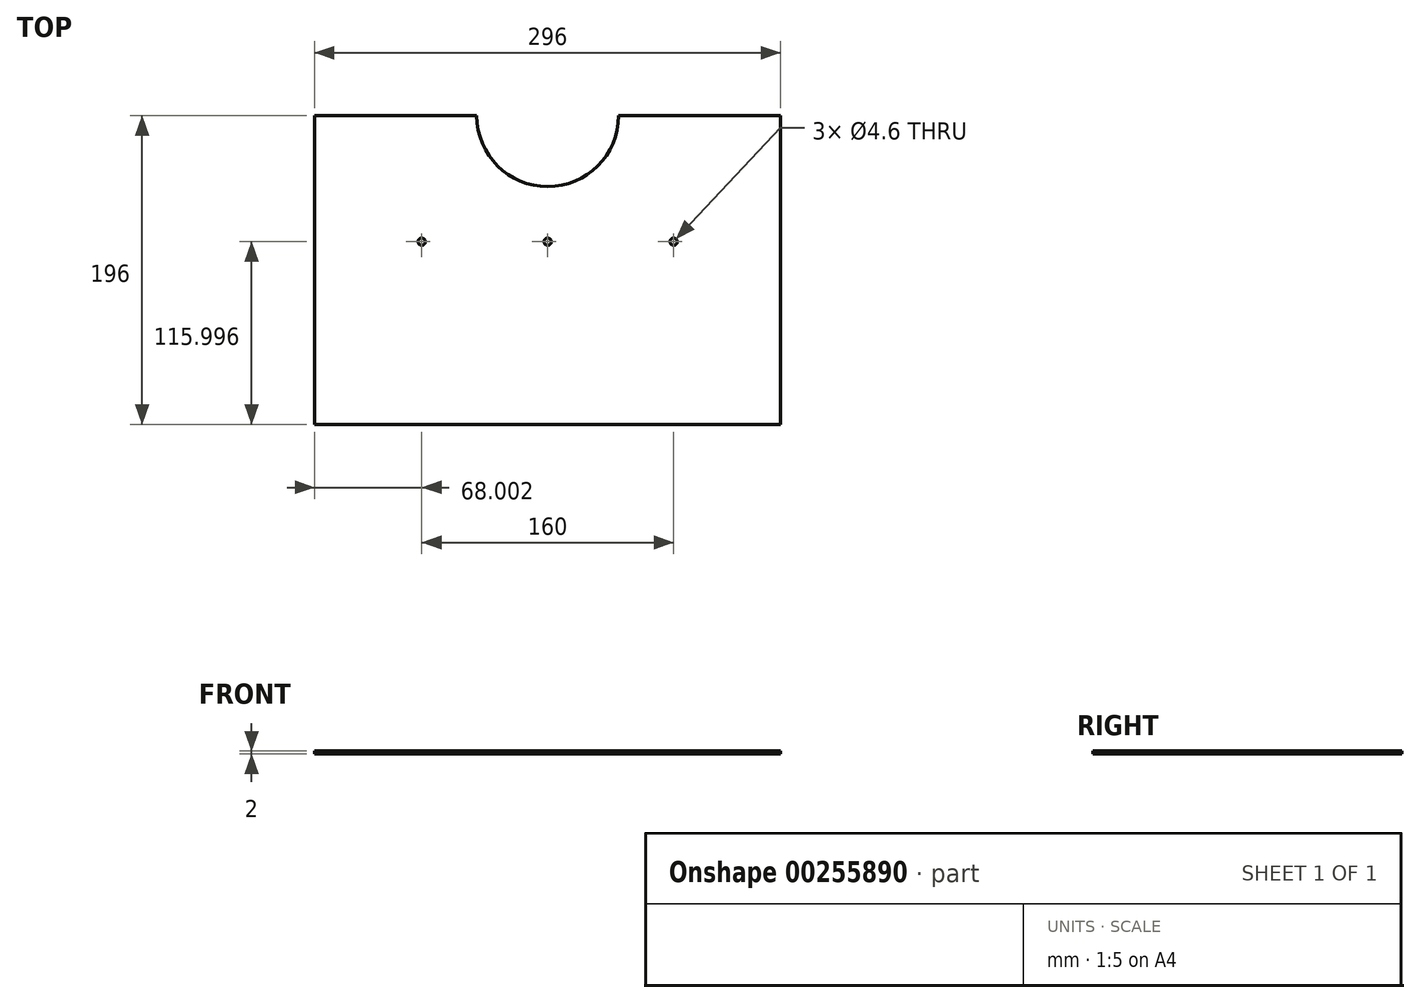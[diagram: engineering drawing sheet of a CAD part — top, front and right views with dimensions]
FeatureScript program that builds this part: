
annotation { "Feature Type Name" : "Feature", "Feature Type Description" : "" }
export const myFeature = defineFeature(function(context is Context, id is Id, definition is map)
    precondition{}
    {
        {
            var Q0;
            Q0=qCreatedBy(makeId("Top.planeOp"),FACE);
            var sketch = newSketch(context, id + "F0", { "sketchPlane" : qUnion([Q0])});
            skLineSegment(sketch, "E0.bottom", {"start": v(-138.47, 114.65) * mm, "end": v(-35.47, 114.65) * mm});
            skLineSegment(sketch, "E0.top", {"start": v(-138.47, -81.35) * mm, "end": v(157.53, -81.35) * mm});
            skLineSegment(sketch, "E0.left", {"start": v(-138.47, 114.65) * mm, "end": v(-138.47, -81.35) * mm});
            skLineSegment(sketch, "E0.right", {"start": v(157.53, 114.65) * mm, "end": v(157.53, -81.35) * mm});
            skPoint(sketch, "E1", {"position": v(-70.47, 34.65) * mm});
            skPoint(sketch, "E2", {"position": v(9.53, 34.65) * mm});
            skPoint(sketch, "E3", {"position": v(89.53, 34.65) * mm});
            skLineSegment(sketch, "E4", {"start": v(-138.47, 34.65) * mm, "end": v(157.53, 34.65) * mm, "construction": true});
            skArc(sketch, "E5", {"start": v(-35.47, 114.65) * mm, "mid": v(9.53, 69.65) * mm, "end": v(54.53, 114.65) * mm});
            skLineSegment(sketch, "E6.trimOffspring", {"start": v(54.53, 114.65) * mm, "end": v(157.53, 114.65) * mm});
            skSolve(sketch);
        }
        {
            var Q0;
            Q0=makeQuery(id+"F0.imprint","IMPRINT",FACE,{"disambiguationData":[TD([[makeQuery(id+"F0.imprint","IMPRINT",EDGE,{"derivedFrom":sQuery(id+"F0.wireOp",EDGE,"E0.bottom")}),-1.0]])]});
            extrude(context, id + "F1", {"entities" : qUnion([Q0]), "depth" : 2 * mm});
        }
        {
            var Q0;
            Q0=sQuery(id+"F0.wireOp",VERTEX,"E1");
            var Q1;
            Q1=sQuery(id+"F0.wireOp",VERTEX,"E2");
            var Q2;
            Q2=sQuery(id+"F0.wireOp",VERTEX,"E3");
            var Q3;
            Q3=makeQuery(id+"F1.opExtrude","SWEPT_BODY",BODY,{"disambiguationData":[OSD([sQuery(id+"F0.wireOp",EDGE,"E0.bottom"),sQuery(id+"F0.wireOp",EDGE,"E0.top"),sQuery(id+"F0.wireOp",EDGE,"E0.left"),sQuery(id+"F0.wireOp",EDGE,"E0.right")])]});
            hole(context, id + "F2", {"style" : HoleStyle.SIMPLE, "endStyle" : HoleEndStyle.THROUGH, "oppositeDirection" : true, "holeDiameter" : 4.6 * mm, "tappedDepth" : 12 * mm, "tapClearance" : 3, "startFromSketch" : true, "locations" : qUnion([Q0, Q1, Q2]), "scope" : qUnion([Q3])});
        }
    });
